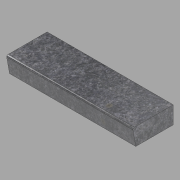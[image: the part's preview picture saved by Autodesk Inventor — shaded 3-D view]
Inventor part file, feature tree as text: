
AUTODESK INVENTOR PART (.ipt)
format: ipt  version: 2022.1 (Build 261234020, 234B)  size: 96,768 bytes
history: native  units: in
note: dims shown in document units (in); Inventor stores cm internally (conversion verified against a paired STEP export)
features: extrude x1, sketch x1
ambient origin geometry x8: Origin, YZ Plane, XZ Plane, XY Plane, X Axis, Y Axis, Z Axis, Center Point
bodies: Solid1 (feature_tree)
feature tree (2):
  extrude  "Extrusion1"  Depth=13.0in
  sketch  "Sketch1"  dims[d0=6.0in d1=13.0in d2=13.5in d3=0.5in d4=43.7083in d5=0.0in]
